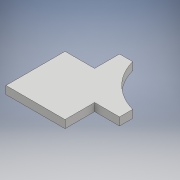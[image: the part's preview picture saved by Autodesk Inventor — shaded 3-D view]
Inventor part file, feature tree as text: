
AUTODESK INVENTOR PART (.ipt)
format: ipt  version: 2018 (Build 220112000, 112)  size: 105,472 bytes
history: native  units: mm
features: other x1, extrude x1, sketch x1
ambient origin geometry x8: Origin, YZ Plane, XZ Plane, XY Plane, X Axis, Y Axis, Z Axis, Center Point
bodies: Body1 (feature_tree)
feature tree (3):
  other  "Bryła1"
  extrude  "Wyciągnięcie proste1"  Depth=45.0mm
  sketch  "Szkic1"
